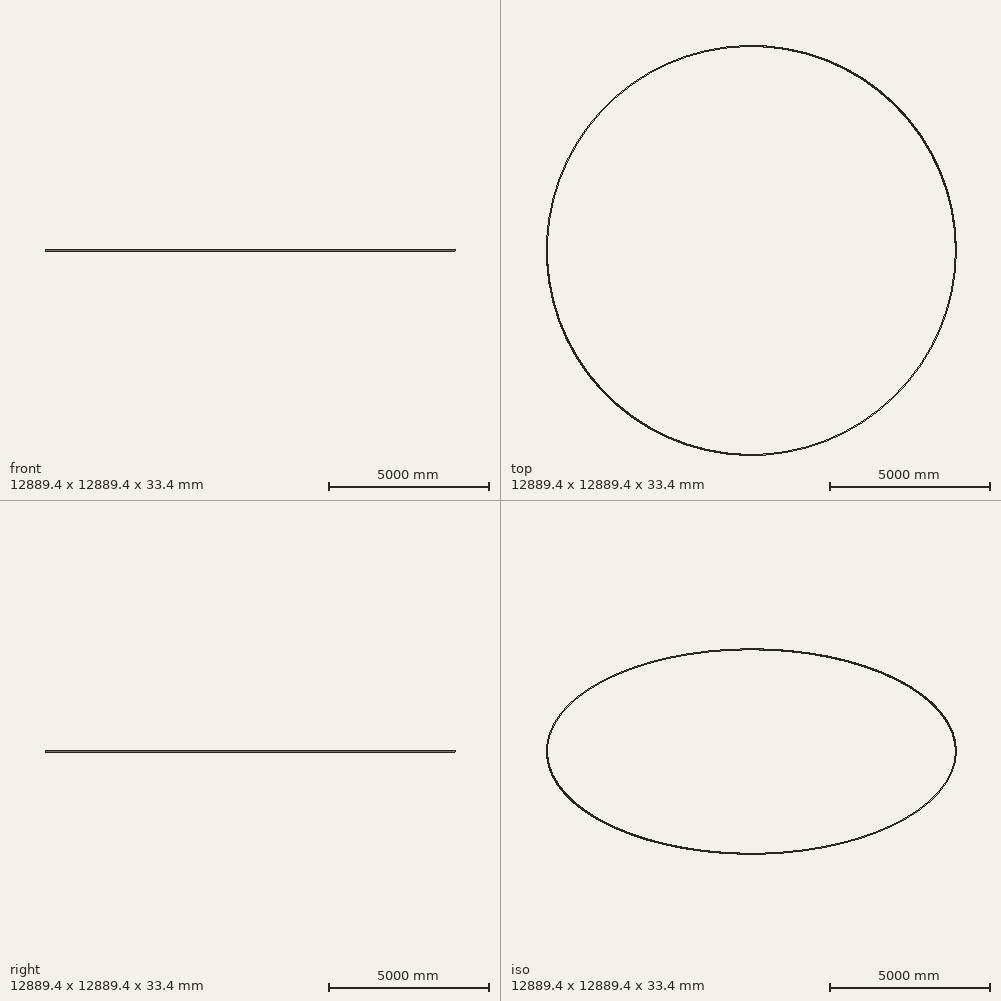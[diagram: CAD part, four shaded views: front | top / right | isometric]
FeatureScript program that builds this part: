
annotation { "Feature Type Name" : "Feature", "Feature Type Description" : "" }
export const myFeature = defineFeature(function(context is Context, id is Id, definition is map)
    precondition{}
    {
        {
            var Q0;
            Q0=qCreatedBy(makeId("Front.planeOp"),FACE);
            var sketch = newSketch(context, id + "F0", { "sketchPlane" : qUnion([Q0])});
            skCircle(sketch, "E0", {"center": v(0, 0) * mm, "radius": 16.7 * mm});
            skCircle(sketch, "E1.0", {"center": v(0, 0) * mm, "radius": 13.93 * mm});
            skLineSegment(sketch, "E2", {"start": v(0, 0) * mm, "end": v(6428, 0) * mm, "construction": true});
            skLineSegment(sketch, "E3", {"start": v(6428, 0) * mm, "end": v(6428, -200) * mm, "construction": true});
            skSolve(sketch);
        }
        {
            var Q0;
            Q0=qSketchRegion(id+"F0",true);
            var Q1;
            Q1=sQuery(id+"F0.wireOp",EDGE,"E3");
            revolve(context, id + "F1", {"surfaceOperationType" : NewSurfaceOperationType.NEW, "entities" : qUnion([Q0]), "axis" : qUnion([Q1]), "revolveType" : RevolveType.FULL});
        }
    });
